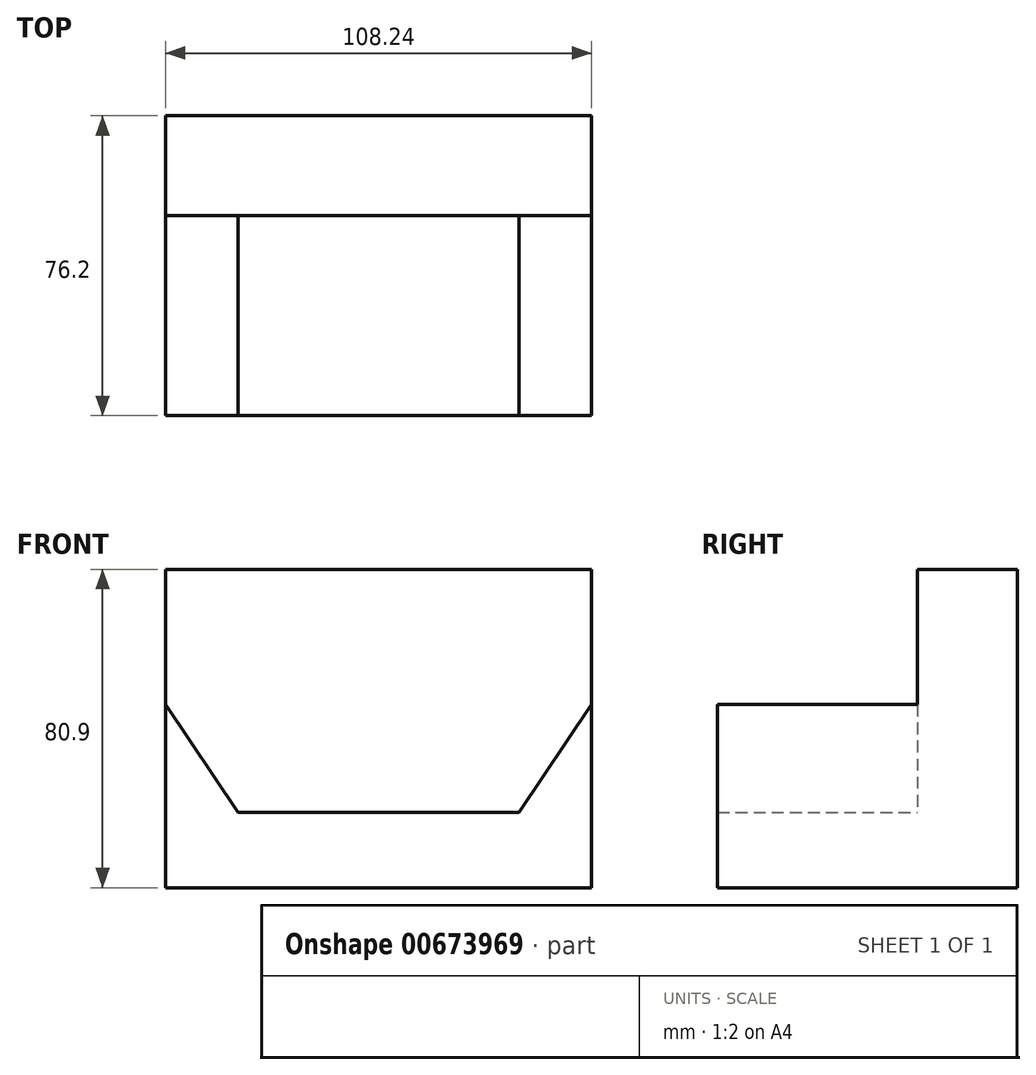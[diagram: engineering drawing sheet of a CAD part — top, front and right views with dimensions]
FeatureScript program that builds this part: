
annotation { "Feature Type Name" : "Feature", "Feature Type Description" : "" }
export const myFeature = defineFeature(function(context is Context, id is Id, definition is map)
    precondition{}
    {
        {
            var Q0;
            Q0=qCreatedBy(makeId("Front.planeOp"),FACE);
            var sketch = newSketch(context, id + "F0", { "sketchPlane" : qUnion([Q0])});
            skLineSegment(sketch, "E0.bottom", {"start": v(54.12, 34.34) * mm, "end": v(-54.12, 34.34) * mm});
            skLineSegment(sketch, "E0.top", {"start": v(54.12, -46.56) * mm, "end": v(-54.12, -46.56) * mm});
            skLineSegment(sketch, "E0.left", {"start": v(54.12, 34.34) * mm, "end": v(54.12, -46.56) * mm});
            skLineSegment(sketch, "E0.right", {"start": v(-54.12, 34.34) * mm, "end": v(-54.12, -46.56) * mm});
            skSolve(sketch);
        }
        {
            var Q0;
            Q0=makeQuery(id+"F0.imprint","IMPRINT",FACE,{"disambiguationData":[TD([[makeQuery(id+"F0.imprint","IMPRINT",EDGE,{"derivedFrom":sQuery(id+"F0.wireOp",EDGE,"E0.bottom")}),1.0]])]});
            extrude(context, id + "F1", {"entities" : qUnion([Q0]), "oppositeDirection" : true, "depth" : 25.4 * mm, "offsetDistance" : 25.4 * mm});
        }
        {
            var Q0;
            Q0=makeQuery(id+"F1.opExtrude","CAP_FACE",FACE,{"disambiguationData":[OSD([sQuery(id+"F0.wireOp",EDGE,"E0.bottom"),sQuery(id+"F0.wireOp",EDGE,"E0.top"),sQuery(id+"F0.wireOp",EDGE,"E0.left"),sQuery(id+"F0.wireOp",EDGE,"E0.right")])],"isStart":true});
            var sketch = newSketch(context, id + "F2", { "sketchPlane" : qUnion([Q0])});
            skLineSegment(sketch, "E1", {"start": v(-54.12, -27.45) * mm, "end": v(54.12, -27.45) * mm});
            skLineSegment(sketch, "E2", {"start": v(54.12, 0) * mm, "end": v(35.67, -27.45) * mm});
            skLineSegment(sketch, "E3", {"start": v(-54.12, 0) * mm, "end": v(-35.67, -27.45) * mm});
            skPoint(sketch, "E3.startSnap0", {"position": v(-54.12, -6.11) * mm});
            skSolve(sketch);
        }
        {
            var Q0;
            {var subQ4=makeQuery(id+"F1.opExtrude","CAP_EDGE",EDGE,{"disambiguationData":[OSD([sQuery(id+"F0.wireOp",EDGE,"E0.top")])],"isStart":true});Q0=makeQuery(id+"F2.imprint","IMPRINT",FACE,{"disambiguationData":[TD([[makeQuery(id+"F2.imprint","IMPRINT",EDGE,{"derivedFrom":subQ4}),-1.0]])]});}
            var Q1;
            {var subQ3=sQuery(id+"F2.wireOp",EDGE,"E3");Q1=makeQuery(id+"F2.imprint","IMPRINT",FACE,{"disambiguationData":[TD([[makeQuery(id+"F2.imprint","IMPRINT",EDGE,{"derivedFrom":subQ3}),-1.0]])]});}
            var Q2;
            {var subQ3=sQuery(id+"F2.wireOp",EDGE,"E2");Q2=makeQuery(id+"F2.imprint","IMPRINT",FACE,{"disambiguationData":[TD([[makeQuery(id+"F2.imprint","IMPRINT",EDGE,{"derivedFrom":subQ3}),1.0]])]});}
            extrude(context, id + "F3", {"entities" : qUnion([Q0, Q1, Q2]), "operationType" : NewBodyOperationType.ADD, "depth" : 50.8 * mm, "offsetDistance" : 25.4 * mm});
        }
    });
